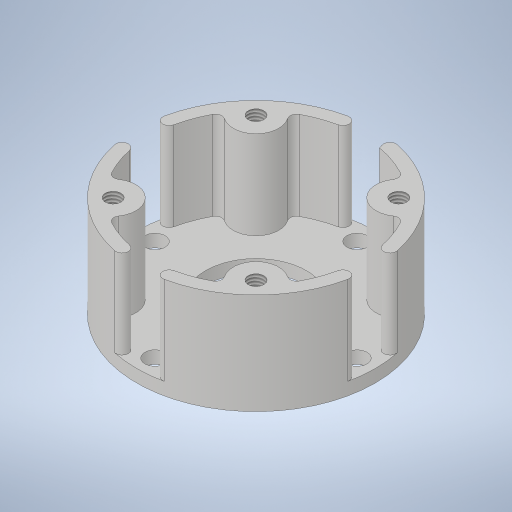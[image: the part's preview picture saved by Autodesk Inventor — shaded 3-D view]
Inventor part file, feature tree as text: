
AUTODESK INVENTOR PART (.ipt)
format: ipt  version: 2023.3 (Build 273359000, 359)  size: 398,848 bytes
history: native  units: in
note: dims shown in document units (in); Inventor stores cm internally (conversion verified against a paired STEP export)
features: sketch x5, extrude x4, projected_geometry x4, hole x2, fillet x1
ambient origin geometry x8: Origin, YZ Plane, XZ Plane, XY Plane, X Axis, Y Axis, Z Axis, Center Point
bodies: Solid1 (feature_tree)
feature tree (16):
  extrude  "Extrusion1"  Depth=2.36in
  hole  "Hole1"  [1 undecoded]
  extrude  "Extrusion2"  Depth=0.125in
  sketch  "Sketch4"  dims[d9=0.201in d10=0.75in d11=0.385in d12=0.25in d13=0.5635in d14=0.536in d15=0.8108in d16=0.125in]
  hole  "Hole2"  [1 undecoded]
  extrude  "Extrusion3"  Depth=1.0in
  fillet  "Fillet1"  Radius=0.375in
  extrude  "Extrusion4"  Depth=1.0in
  sketch  "Sketch1"  dims[d0=2.0in d1=2.36in]
  sketch  "Sketch2"  dims[d2=0.125in d3=0.0in d4=2.0in]
  sketch  "Sketch3"  dims[d5=3.1496in d7=360.0deg]
  projected_geometry  "Projected Loop1"
  projected_geometry  "Projected Loop2"
  projected_geometry  "Projected Loop3"
  projected_geometry  "Projected Loop4"
  sketch  "Sketch5"  dims[d25=0.875in d26=0.0in d27=0.156in d28=0.38in d29=0.375in d30=0.25in d31=0.5635in d32=1.0in d33=0.8108in d34=0.375in d35=0.375in d36=0.375in d37=0.375in d38=0.0in d39=0.0in d40=0.0625in d41=2.008in d42=1.0in d43=0.0in d44=0.0in]
note: 2 required parameter values undecoded (feature->parameter linkage not recoverable at this tier; creation-order binding heuristic only, values carry confidence <= 0.55)
